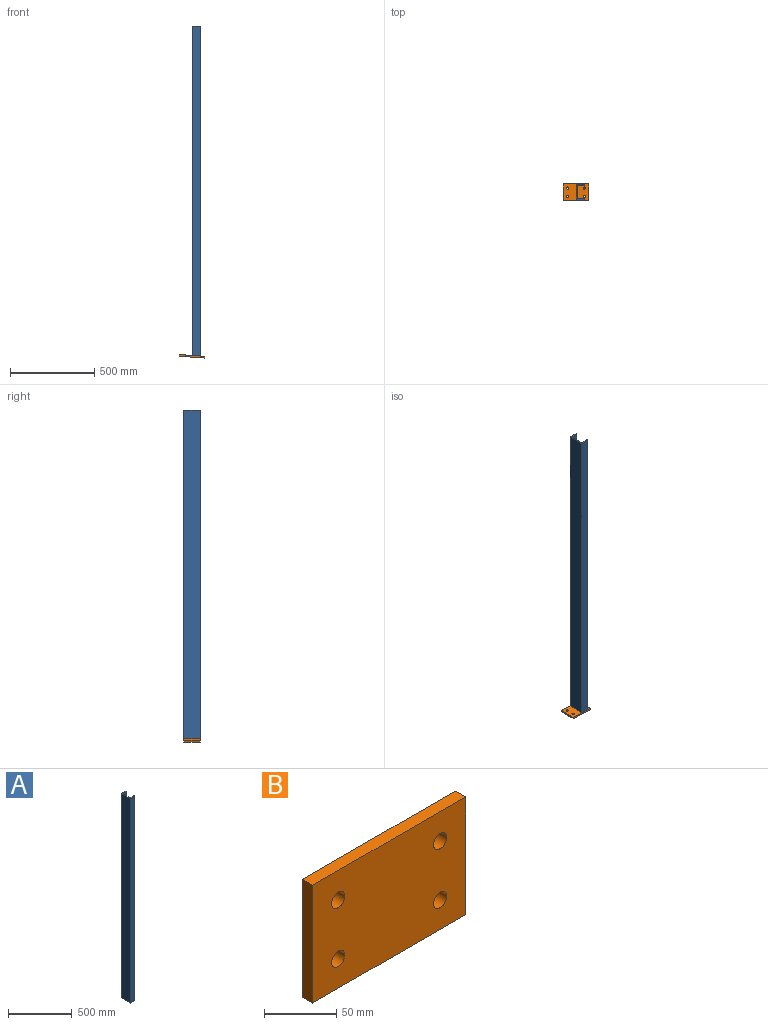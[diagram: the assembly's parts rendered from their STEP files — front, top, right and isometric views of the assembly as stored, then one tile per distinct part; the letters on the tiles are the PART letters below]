
ASSEMBLY  parts=2 mates=1
PART A: 14 faces, bbox 50x100x1958.1 mm
  f0: plane 1958.11x50mm, normal (0,1,0), area 97819.7mm2, adj f9,f10,f12,f13
  f1: cylinder r=4.5mm len=1958.11mm, axis (0,0,1), area 13840.3mm2, adj f2,f10,f12,f13
  f2: plane 1957.8x31mm, normal (0.06,-1,0), area 60785mm2, adj f1,f3,f12,f13
  f3: cylinder r=8.5mm len=1955.67mm, axis (0,0,1), area 26106.7mm2, adj f2,f4,f12,f13
  f4: plane 1955.09x64mm, normal (1,0,0), area 125125.8mm2, adj f3,f5,f12,f13
  f5: cylinder r=8.5mm len=1955.67mm, axis (0,0,1), area 26106.7mm2, adj f4,f6,f12,f13
  f6: plane 1957.8x31mm, normal (0.06,1,0), area 60785mm2, adj f5,f7,f12,f13
  f7: cylinder r=4.5mm len=1958.11mm, axis (0,0,1), area 13840.3mm2, adj f6,f11,f12,f13
  f8: plane 1958.11x50mm, normal (0,-1,0), area 97819.7mm2, adj f9,f11,f12,f13
  f9: plane 1954.68x100mm, normal (-1,0,0), area 195467.9mm2, adj f0,f8,f12,f13
  f10: plane 1958.11x3mm, normal (1,0,0), area 5874.3mm2, adj f0,f1,f12,f13
  f11: plane 1958.11x3mm, normal (1,0,0), area 5874.3mm2, adj f7,f8,f12,f13
  f12: plane 100x50mm, normal (0,0,1), area 1378.3mm2, adj f0,f1,f2,f3,f4,f5,f6,f7
  f13: plane 100x50mm, normal (-0.07,0,-1), area 1381.6mm2, adj f0,f1,f2,f3,f4,f5,f6,f7
PART B: 10 faces, bbox 150x10x100 mm
  f0: plane 150x10mm, normal (0,0,-1), area 1500mm2, adj f1,f7,f8,f9
  f1: plane 100x10mm, normal (1,0,0), area 1000mm2, adj f0,f2,f8,f9
  f2: plane 150x10mm, normal (0,0,1), area 1500mm2, adj f1,f7,f8,f9
  f3: cylinder r=6.5mm len=13mm, axis (0,1,0), area 408.4mm2, adj f8,f9
  f4: cylinder r=6.5mm len=13mm, axis (0,1,0), area 408.4mm2, adj f8,f9
  f5: cylinder r=6.5mm len=13mm, axis (0,1,0), area 408.4mm2, adj f8,f9
  f6: cylinder r=6.5mm len=13mm, axis (0,1,0), area 408.4mm2, adj f8,f9
  f7: plane 100x10mm, normal (-1,0,0), area 1000mm2, adj f0,f2,f8,f9
  f8: plane 150x100mm, normal (0,-1,0), area 14469.1mm2, adj f0,f1,f2,f3,f4,f5,f6,f7
  f9: plane 150x100mm, normal (0,1,0), area 14469.1mm2, adj f0,f1,f2,f3,f4,f5,f6,f7
PLACE A t=(-388.22,-198.12,-886.58)mm
PLACE B rot(axis=(-1,0.03,0.03),90.1deg) t=(-388.54,-148.04,-888.13)mm
MATE fastened B.f8 <-> A.f13  axis (0.07,0,1) through (-388.2,-148.04,-883.15)mm
